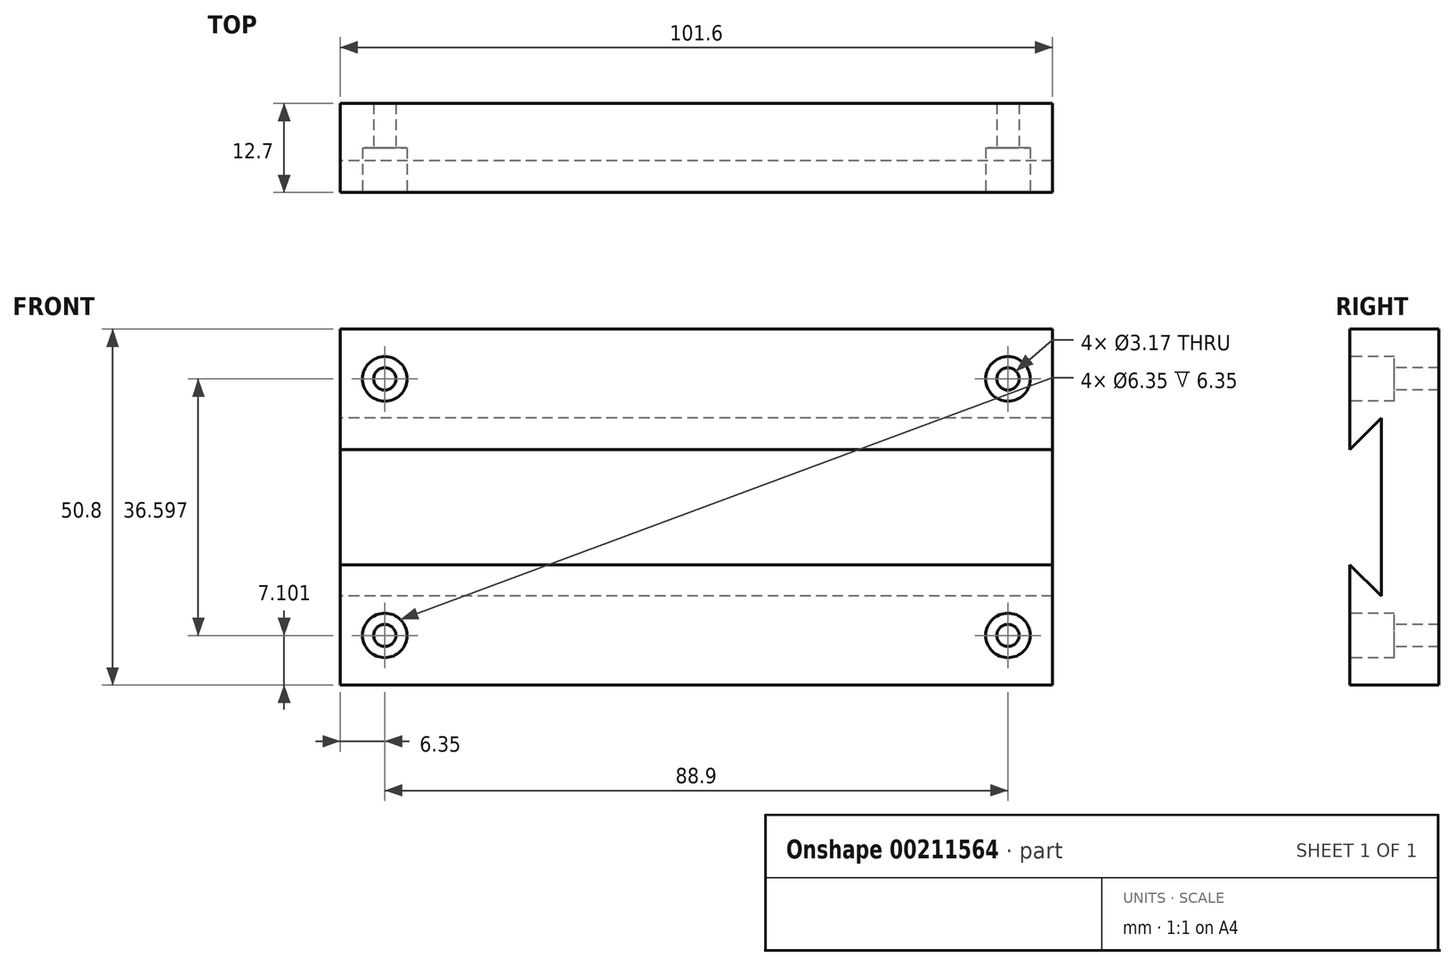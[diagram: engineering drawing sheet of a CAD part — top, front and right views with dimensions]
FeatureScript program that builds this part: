
annotation { "Feature Type Name" : "Feature", "Feature Type Description" : "" }
export const myFeature = defineFeature(function(context is Context, id is Id, definition is map)
    precondition{}
    {
        {
            var Q0;
            Q0=qCreatedBy(makeId("Front.planeOp"),FACE);
            var sketch = newSketch(context, id + "F0", { "sketchPlane" : qUnion([Q0])});
            skLineSegment(sketch, "E0.bottom", {"start": v(0, 0) * mm, "end": v(101.6, 0) * mm});
            skLineSegment(sketch, "E0.top", {"start": v(0, 50.8) * mm, "end": v(101.6, 50.8) * mm});
            skLineSegment(sketch, "E0.left", {"start": v(0, 0) * mm, "end": v(0, 50.8) * mm});
            skLineSegment(sketch, "E0.right", {"start": v(101.6, 0) * mm, "end": v(101.6, 50.8) * mm});
            skSolve(sketch);
        }
        {
            var Q0;
            Q0=makeQuery(id+"F0.imprint","IMPRINT",FACE,{"disambiguationData":[TD([[makeQuery(id+"F0.imprint","IMPRINT",EDGE,{"derivedFrom":sQuery(id+"F0.wireOp",EDGE,"E0.bottom")}),1.0]])]});
            extrude(context, id + "F1", {"entities" : qUnion([Q0]), "depth" : 12.7 * mm});
        }
        {
            var Q0;
            Q0=makeQuery(id+"F1.opExtrude","CAP_FACE",FACE,{"disambiguationData":[OSD([sQuery(id+"F0.wireOp",EDGE,"E0.bottom"),sQuery(id+"F0.wireOp",EDGE,"E0.top"),sQuery(id+"F0.wireOp",EDGE,"E0.left"),sQuery(id+"F0.wireOp",EDGE,"E0.right")])],"isStart":false});
            var sketch = newSketch(context, id + "F2", { "sketchPlane" : qUnion([Q0])});
            skPoint(sketch, "E1", {"position": v(6.35, 7.1) * mm});
            skPoint(sketch, "E2.MirrorP", {"position": v(6.35, 43.7) * mm});
            skPoint(sketch, "E3.MirrorP", {"position": v(95.25, 7.1) * mm});
            skPoint(sketch, "E4.MirrorP", {"position": v(95.25, 43.7) * mm});
            skSolve(sketch);
        }
        {
            var Q0;
            Q0=sQuery(id+"F2.wireOp",VERTEX,"E1");
            var Q1;
            Q1=makeQuery(id+"F1.opExtrude","SWEPT_BODY",BODY,{"disambiguationData":[OSD([sQuery(id+"F0.wireOp",EDGE,"E0.bottom"),sQuery(id+"F0.wireOp",EDGE,"E0.top"),sQuery(id+"F0.wireOp",EDGE,"E0.left"),sQuery(id+"F0.wireOp",EDGE,"E0.right")])]});
            hole(context, id + "F3", {"style" : HoleStyle.C_BORE, "endStyle" : HoleEndStyle.THROUGH, "holeDiameter" : 3.17 * mm, "cBoreDiameter" : 6.35 * mm, "cBoreDepth" : 6.35 * mm, "locations" : qUnion([Q0]), "scope" : qUnion([Q1]), "isTappedThrough" : true});
        }
        {
            var Q0;
            Q0=makeQuery(id+"F1.opExtrude","SWEPT_FACE",FACE,{"disambiguationData":[OSD([sQuery(id+"F0.wireOp",EDGE,"E0.left")])]});
            var sketch = newSketch(context, id + "F4", { "sketchPlane" : qUnion([Q0])});
            skLineSegment(sketch, "E5", {"start": v(8.2, 38.1) * mm, "end": v(8.2, 12.7) * mm});
            skLineSegment(sketch, "E6", {"start": v(8.2, 12.7) * mm, "end": v(12.7, 17.2) * mm});
            skLineSegment(sketch, "E7", {"start": v(8.2, 38.1) * mm, "end": v(12.7, 33.6) * mm});
            skSolve(sketch);
        }
        {
            var Q0;
            Q0=makeQuery(id+"F4.imprint","IMPRINT",FACE,{"disambiguationData":[TD([[makeQuery(id+"F4.imprint","IMPRINT",EDGE,{"derivedFrom":sQuery(id+"F4.wireOp",EDGE,"E5")}),1.0]])]});
            extrude(context, id + "F5", {"entities" : qUnion([Q0]), "operationType" : NewBodyOperationType.REMOVE, "endBound" : BoundingType.THROUGH_ALL, "oppositeDirection" : true, "depth" : 25.4 * mm});
        }
        {
            var Q0;
            Q0=sQuery(id+"F2.wireOp",VERTEX,"E2.MirrorP");
            var Q1;
            Q1=makeQuery(id+"F1.opExtrude","SWEPT_BODY",BODY,{"disambiguationData":[OSD([sQuery(id+"F0.wireOp",EDGE,"E0.bottom"),sQuery(id+"F0.wireOp",EDGE,"E0.top"),sQuery(id+"F0.wireOp",EDGE,"E0.left"),sQuery(id+"F0.wireOp",EDGE,"E0.right")])]});
            hole(context, id + "F6", {"style" : HoleStyle.C_BORE, "endStyle" : HoleEndStyle.THROUGH, "holeDiameter" : 3.17 * mm, "cBoreDiameter" : 6.35 * mm, "cBoreDepth" : 6.35 * mm, "locations" : qUnion([Q0]), "scope" : qUnion([Q1]), "isTappedThrough" : true});
        }
        {
            var Q0;
            Q0=sQuery(id+"F2.wireOp",VERTEX,"E4.MirrorP");
            var Q1;
            Q1=makeQuery(id+"F1.opExtrude","SWEPT_BODY",BODY,{"disambiguationData":[OSD([sQuery(id+"F0.wireOp",EDGE,"E0.bottom"),sQuery(id+"F0.wireOp",EDGE,"E0.top"),sQuery(id+"F0.wireOp",EDGE,"E0.left"),sQuery(id+"F0.wireOp",EDGE,"E0.right")])]});
            hole(context, id + "F7", {"style" : HoleStyle.C_BORE, "endStyle" : HoleEndStyle.THROUGH, "holeDiameter" : 3.17 * mm, "cBoreDiameter" : 6.35 * mm, "cBoreDepth" : 6.35 * mm, "locations" : qUnion([Q0]), "scope" : qUnion([Q1]), "isTappedThrough" : true});
        }
        {
            var Q0;
            Q0=sQuery(id+"F2.wireOp",VERTEX,"E3.MirrorP");
            var Q1;
            Q1=makeQuery(id+"F1.opExtrude","SWEPT_BODY",BODY,{"disambiguationData":[OSD([sQuery(id+"F0.wireOp",EDGE,"E0.bottom"),sQuery(id+"F0.wireOp",EDGE,"E0.top"),sQuery(id+"F0.wireOp",EDGE,"E0.left"),sQuery(id+"F0.wireOp",EDGE,"E0.right")])]});
            hole(context, id + "F8", {"style" : HoleStyle.C_BORE, "endStyle" : HoleEndStyle.THROUGH, "holeDiameter" : 3.17 * mm, "cBoreDiameter" : 6.35 * mm, "cBoreDepth" : 6.35 * mm, "locations" : qUnion([Q0]), "scope" : qUnion([Q1]), "isTappedThrough" : true});
        }
    });
